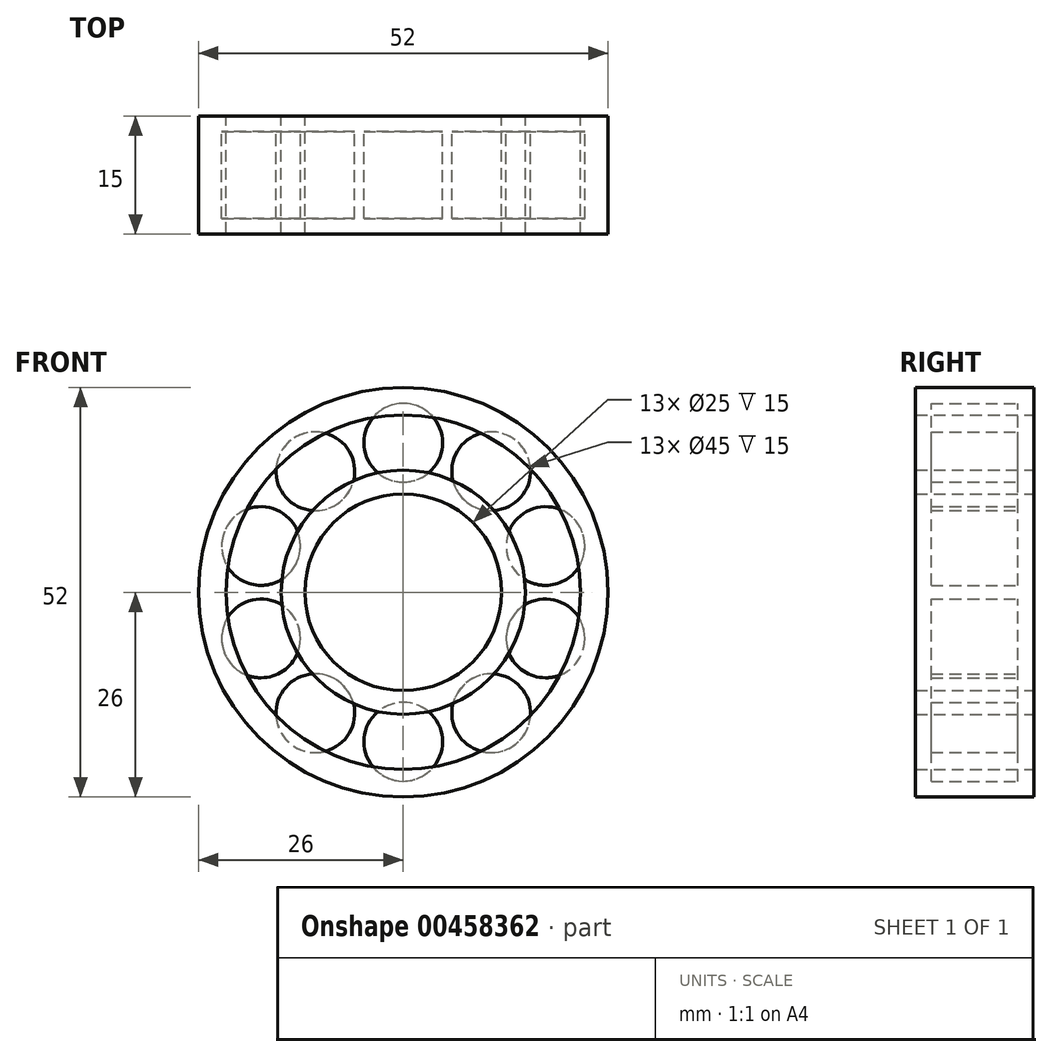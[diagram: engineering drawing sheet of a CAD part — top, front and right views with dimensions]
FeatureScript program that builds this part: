
annotation { "Feature Type Name" : "Feature", "Feature Type Description" : "" }
export const myFeature = defineFeature(function(context is Context, id is Id, definition is map)
    precondition{}
    {
        {
            var Q0;
            Q0=qCreatedBy(makeId("Front.planeOp"),FACE);
            cPlane(context, id + "F0", {"entities" : qUnion([Q0]), "cplaneType" : CPlaneType.OFFSET, "offset" : 2 * mm, "width" : 150 * mm, "height" : 150 * mm});
        }
        {
            var Q0;
            Q0=qCreatedBy(makeId("Front.planeOp"),FACE);
            var sketch = newSketch(context, id + "F1", { "sketchPlane" : qUnion([Q0])});
            skCircle(sketch, "E0", {"center": v(0, 0) * mm, "radius": 15.5 * mm});
            skCircle(sketch, "E1", {"center": v(0, 0) * mm, "radius": 12.5 * mm});
            skSolve(sketch);
        }
        {
            var Q0;
            Q0=qCreatedBy(makeId("Front.planeOp"),FACE);
            var sketch = newSketch(context, id + "F2", { "sketchPlane" : qUnion([Q0])});
            skCircle(sketch, "E2", {"center": v(0, 0) * mm, "radius": 26 * mm});
            skCircle(sketch, "E3", {"center": v(0, 0) * mm, "radius": 22.5 * mm});
            skSolve(sketch);
        }
        {
            var Q0;
            Q0=qCreatedBy(id+"F0.planeOp",FACE);
            var sketch = newSketch(context, id + "F3", { "sketchPlane" : qUnion([Q0])});
            skCircle(sketch, "E4", {"center": v(0, 19) * mm, "radius": 5 * mm});
            skCircle(sketch, "E5.1.0", {"center": v(-11.17, 15.37) * mm, "radius": 5 * mm});
            skCircle(sketch, "E5.2.0", {"center": v(-18.07, 5.87) * mm, "radius": 5 * mm});
            skCircle(sketch, "E5.3.0", {"center": v(-18.07, -5.87) * mm, "radius": 5 * mm});
            skCircle(sketch, "E5.4.0", {"center": v(-11.17, -15.37) * mm, "radius": 5 * mm});
            skCircle(sketch, "E5.5.0", {"center": v(0, -19) * mm, "radius": 5 * mm});
            skCircle(sketch, "E5.6.0", {"center": v(11.17, -15.37) * mm, "radius": 5 * mm});
            skCircle(sketch, "E5.7.0", {"center": v(18.07, -5.87) * mm, "radius": 5 * mm});
            skCircle(sketch, "E5.8.0", {"center": v(18.07, 5.87) * mm, "radius": 5 * mm});
            skCircle(sketch, "E5.9.0", {"center": v(11.17, 15.37) * mm, "radius": 5 * mm});
            skPoint(sketch, "E5.center", {"position": v(0, 0) * mm});
            skSolve(sketch);
        }
        {
            var Q0;
            Q0 = qSketchRegion(id + "F3", true);
            extrude(context, id + "F4", {"entities" : qUnion([Q0]), "depth" : 11 * mm});
        }
        {
            var Q0;
            Q0 = qSketchRegion(id + "F1", true);
            extrude(context, id + "F5", {"entities" : qUnion([Q0]), "depth" : 15 * mm});
        }
        {
            var Q0;
            Q0 = qSketchRegion(id + "F2", true);
            extrude(context, id + "F6", {"entities" : qUnion([Q0]), "depth" : 15 * mm});
        }
    });
